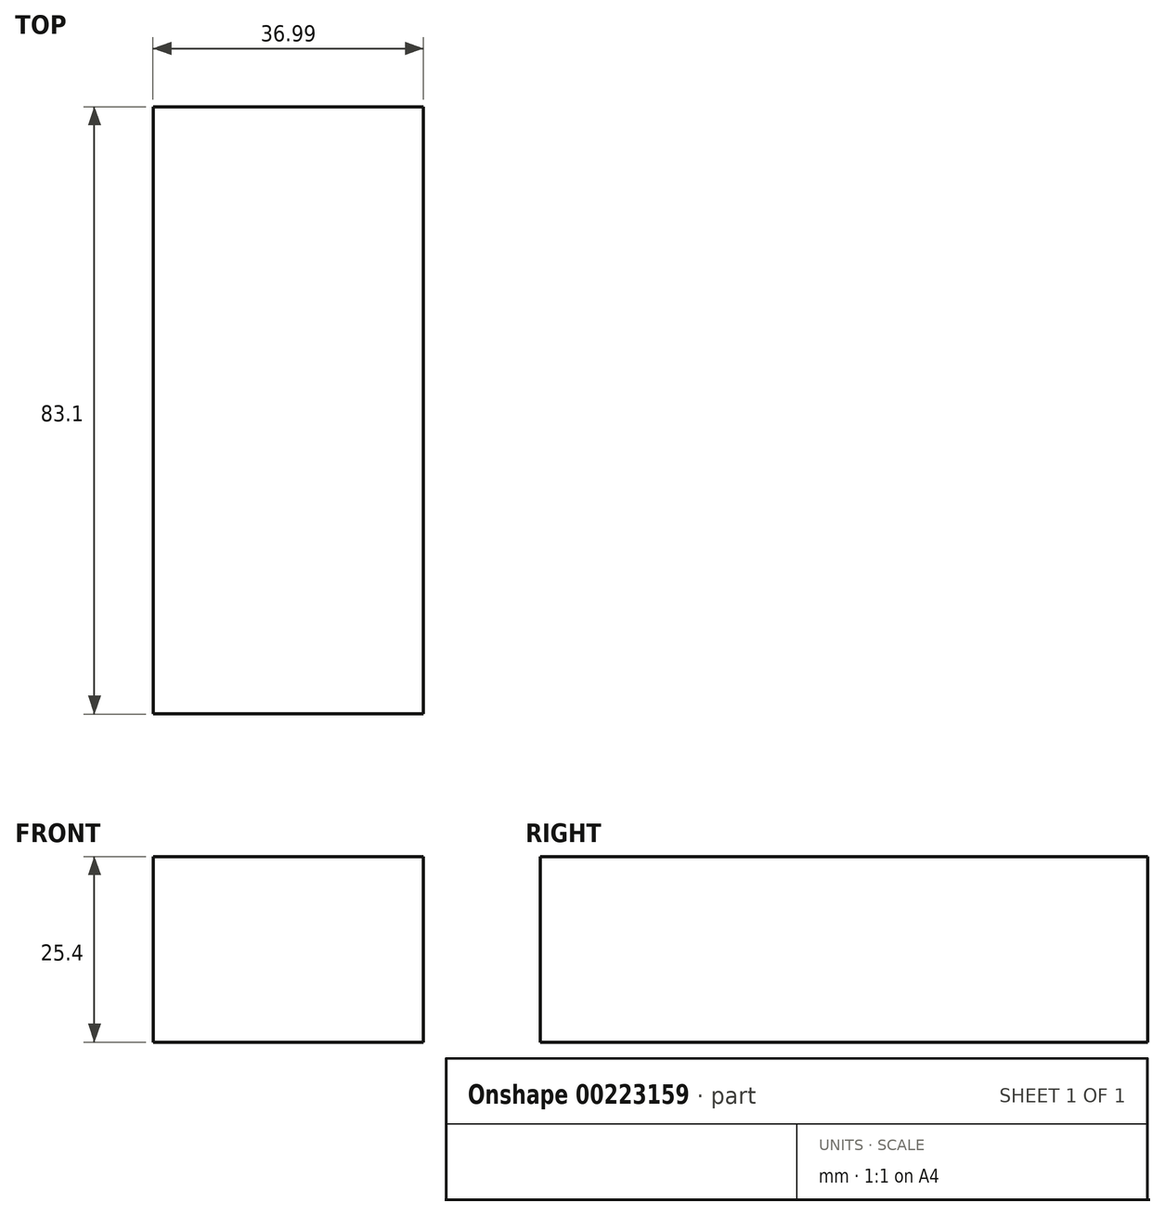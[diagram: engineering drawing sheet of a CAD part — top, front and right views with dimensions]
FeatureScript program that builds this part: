
annotation { "Feature Type Name" : "Feature", "Feature Type Description" : "" }
export const myFeature = defineFeature(function(context is Context, id is Id, definition is map)
    precondition{}
    {
        {
            var Q0;
            Q0=qCreatedBy(makeId("Top.planeOp"),FACE);
            var sketch = newSketch(context, id + "F0", { "sketchPlane" : qUnion([Q0])});
            skLineSegment(sketch, "E0.bottom", {"start": v(-106.1, 76.4) * mm, "end": v(-143.08, 76.4) * mm});
            skLineSegment(sketch, "E0.top", {"start": v(-106.1, -6.7) * mm, "end": v(-143.08, -6.7) * mm});
            skLineSegment(sketch, "E0.left", {"start": v(-106.1, 76.4) * mm, "end": v(-106.1, -6.7) * mm});
            skLineSegment(sketch, "E0.right", {"start": v(-143.08, 76.4) * mm, "end": v(-143.08, -6.7) * mm});
            skSolve(sketch);
        }
        {
            var Q0;
            Q0 = qSketchRegion(id + "F0", true);
            extrude(context, id + "F1", {"entities" : qUnion([Q0]), "depth" : 25.4 * mm});
        }
    });
